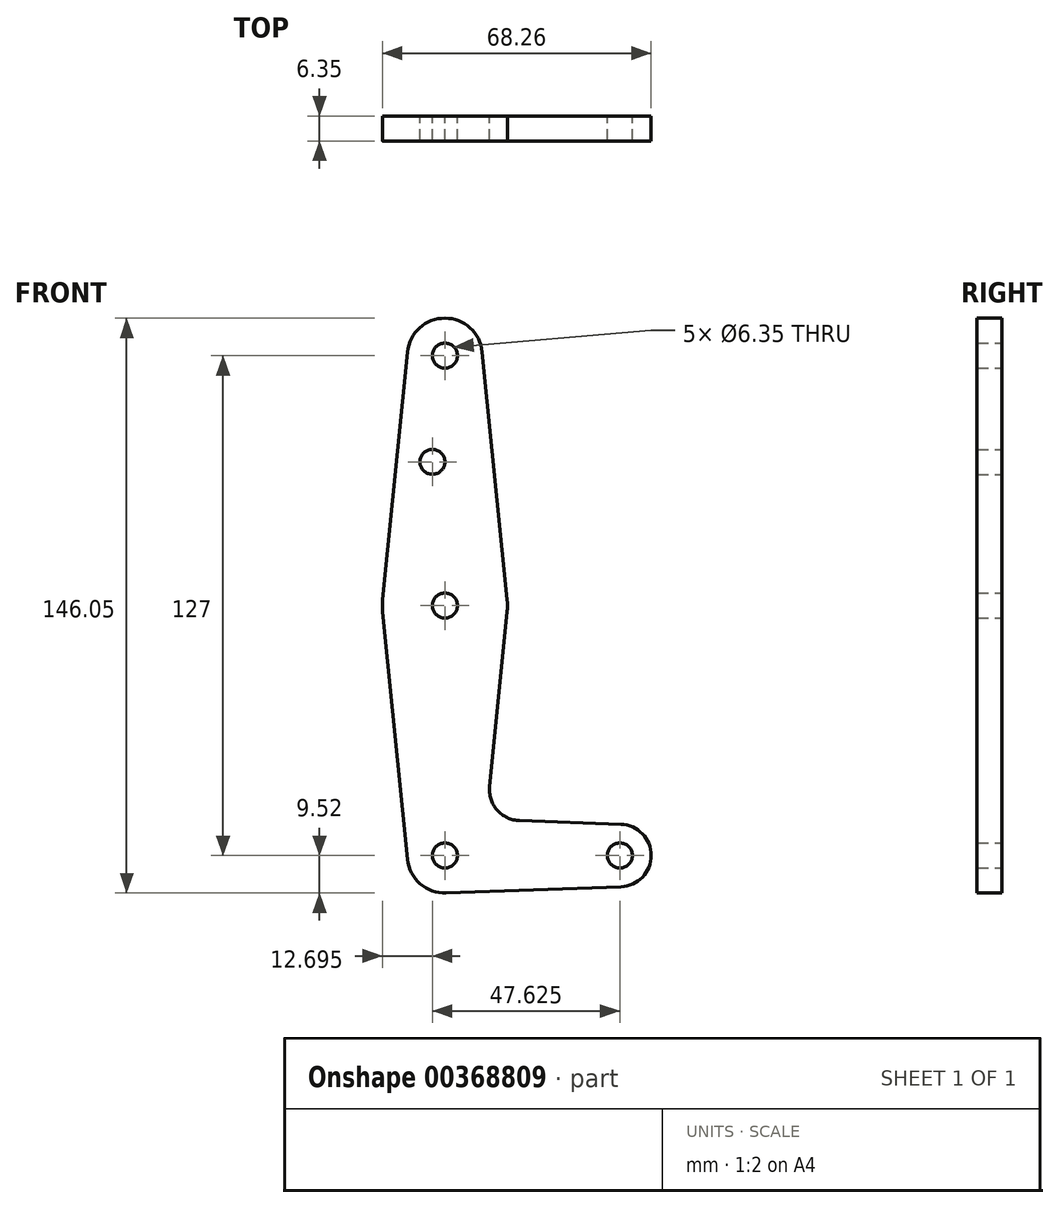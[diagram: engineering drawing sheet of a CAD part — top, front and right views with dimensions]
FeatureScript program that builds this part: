
annotation { "Feature Type Name" : "Feature", "Feature Type Description" : "" }
export const myFeature = defineFeature(function(context is Context, id is Id, definition is map)
    precondition{}
    {
        {
            var Q0;
            Q0=qCreatedBy(makeId("Front.planeOp"),FACE);
            var sketch = newSketch(context, id + "F0", { "sketchPlane" : qUnion([Q0])});
            skLineSegment(sketch, "E0", {"start": v(0, 0) * mm, "end": v(0, 127) * mm});
            skLineSegment(sketch, "E1", {"start": v(0, 0) * mm, "end": v(44.45, 0) * mm});
            skCircle(sketch, "E2", {"center": v(0, 127) * mm, "radius": 9.53 * mm});
            skCircle(sketch, "E3", {"center": v(0, 127) * mm, "radius": 3.18 * mm});
            skCircle(sketch, "E4", {"center": v(0, 63.5) * mm, "radius": 15.88 * mm});
            skCircle(sketch, "E5", {"center": v(0, 0) * mm, "radius": 9.53 * mm});
            skCircle(sketch, "E6", {"center": v(44.45, 0) * mm, "radius": 7.94 * mm});
            skLineSegment(sketch, "E7", {"start": v(9.48, 127.95) * mm, "end": v(15.8, 65.09) * mm});
            skLineSegment(sketch, "E8", {"start": v(-9.48, 127.95) * mm, "end": v(-15.8, 65.09) * mm});
            skLineSegment(sketch, "E9", {"start": v(-15.8, 61.91) * mm, "end": v(-9.48, -0.95) * mm});
            skLineSegment(sketch, "E10", {"start": v(15.8, 61.91) * mm, "end": v(11.34, 17.6) * mm});
            skLineSegment(sketch, "E11", {"start": v(18.97, 8.85) * mm, "end": v(44.73, 7.93) * mm});
            skLineSegment(sketch, "E12", {"start": v(0.34, -9.52) * mm, "end": v(44.73, -7.93) * mm});
            skCircle(sketch, "E13", {"center": v(0, 63.5) * mm, "radius": 3.18 * mm});
            skCircle(sketch, "E14", {"center": v(0, 0) * mm, "radius": 3.18 * mm});
            skCircle(sketch, "E15", {"center": v(44.45, 0) * mm, "radius": 3.18 * mm});
            skArc(sketch, "E16.filletArc", {"start": v(11.34, 17.6) * mm, "mid": v(13.26, 11.57) * mm, "end": v(18.97, 8.85) * mm});
            skCircle(sketch, "E17", {"center": v(-3.17, 100.03) * mm, "radius": 3.18 * mm});
            skSolve(sketch);
        }
        {
            var Q0;
            Q0=makeQuery(id+"F0.imprint","IMPRINT",FACE,{"disambiguationData":[TD([[makeQuery(id+"F0.imprint","IMPRINT",EDGE,{"derivedFrom":sQuery(id+"F0.wireOp",EDGE,"E3")}),-1.0]])]});
            var Q1;
            {var subQ0=sQuery(id+"F0.wireOp",EDGE,"E8");Q1=makeQuery(id+"F0.imprint","IMPRINT",FACE,{"disambiguationData":[TD([[makeQuery(id+"F0.imprint","IMPRINT",EDGE,{"derivedFrom":subQ0}),1.0]])]});}
            var Q2;
            {var subQ0=sQuery(id+"F0.wireOp",EDGE,"E7");Q2=makeQuery(id+"F0.imprint","IMPRINT",FACE,{"disambiguationData":[TD([[makeQuery(id+"F0.imprint","IMPRINT",EDGE,{"derivedFrom":subQ0}),-1.0]])]});}
            var Q3;
            {var subQ0=sQuery(id+"F0.wireOp",EDGE,"E4");var subQ3=sQuery(id+"F0.wireOp",EDGE,"E0");var subQ7=makeQuery(id+"F0.imprint","INTERSECT",VERTEX,{"disambiguationData":[OD(0.0)],"derivedFrom":[subQ3,subQ0]});Q3=makeQuery(id+"F0.imprint","IMPRINT",FACE,{"disambiguationData":[TD([[makeQuery(id+"F0.imprint","IMPRINT",EDGE,{"disambiguationData":[TD([[subQ7,-1.0]])],"derivedFrom":subQ3}),1.0]])]});}
            var Q4;
            {var subQ0=sQuery(id+"F0.wireOp",EDGE,"E4");var subQ2=sQuery(id+"F0.wireOp",EDGE,"E0");var subQ3=makeQuery(id+"F0.imprint","INTERSECT",VERTEX,{"disambiguationData":[OD(0.0)],"derivedFrom":[subQ2,subQ0]});Q4=makeQuery(id+"F0.imprint","IMPRINT",FACE,{"disambiguationData":[TD([[makeQuery(id+"F0.imprint","IMPRINT",EDGE,{"disambiguationData":[TD([[subQ3,-1.0]])],"derivedFrom":subQ2}),-1.0]])]});}
            var Q5;
            {var subQ5=sQuery(id+"F0.wireOp",EDGE,"E9");Q5=makeQuery(id+"F0.imprint","IMPRINT",FACE,{"disambiguationData":[TD([[makeQuery(id+"F0.imprint","IMPRINT",EDGE,{"derivedFrom":subQ5}),1.0]])]});}
            var Q6;
            {var subQ8=sQuery(id+"F0.wireOp",EDGE,"E10");Q6=makeQuery(id+"F0.imprint","IMPRINT",FACE,{"disambiguationData":[TD([[makeQuery(id+"F0.imprint","IMPRINT",EDGE,{"derivedFrom":subQ8}),-1.0]])]});}
            var Q7;
            {var subQ3=sQuery(id+"F0.wireOp",EDGE,"E14");var subQ4=sQuery(id+"F0.wireOp",EDGE,"E0");var subQ5=makeQuery(id+"F0.imprint","INTERSECT",VERTEX,{"derivedFrom":[subQ4,subQ3]});Q7=makeQuery(id+"F0.imprint","IMPRINT",FACE,{"disambiguationData":[TD([[makeQuery(id+"F0.imprint","IMPRINT",EDGE,{"disambiguationData":[TD([[subQ5,-1.0]])],"derivedFrom":subQ4}),1.0]])]});}
            var Q8;
            {var subQ0=sQuery(id+"F0.wireOp",EDGE,"E14");var subQ1=sQuery(id+"F0.wireOp",EDGE,"E0");var subQ2=makeQuery(id+"F0.imprint","INTERSECT",VERTEX,{"derivedFrom":[subQ1,subQ0]});Q8=makeQuery(id+"F0.imprint","IMPRINT",FACE,{"disambiguationData":[TD([[makeQuery(id+"F0.imprint","IMPRINT",EDGE,{"disambiguationData":[TD([[subQ2,-1.0]])],"derivedFrom":subQ1}),-1.0]])]});}
            var Q9;
            {var subQ5=sQuery(id+"F0.wireOp",EDGE,"E12");Q9=makeQuery(id+"F0.imprint","IMPRINT",FACE,{"disambiguationData":[TD([[makeQuery(id+"F0.imprint","IMPRINT",EDGE,{"derivedFrom":subQ5}),1.0]])]});}
            var Q10;
            Q10=makeQuery(id+"F0.imprint","IMPRINT",FACE,{"disambiguationData":[TD([[makeQuery(id+"F0.imprint","IMPRINT",EDGE,{"derivedFrom":sQuery(id+"F0.wireOp",EDGE,"E15")}),-1.0]])]});
            extrude(context, id + "F1", {"entities" : qUnion([Q0, Q1, Q2, Q3, Q4, Q5, Q6, Q7, Q8, Q9, Q10]), "depth" : 6.35 * mm});
        }
    });
